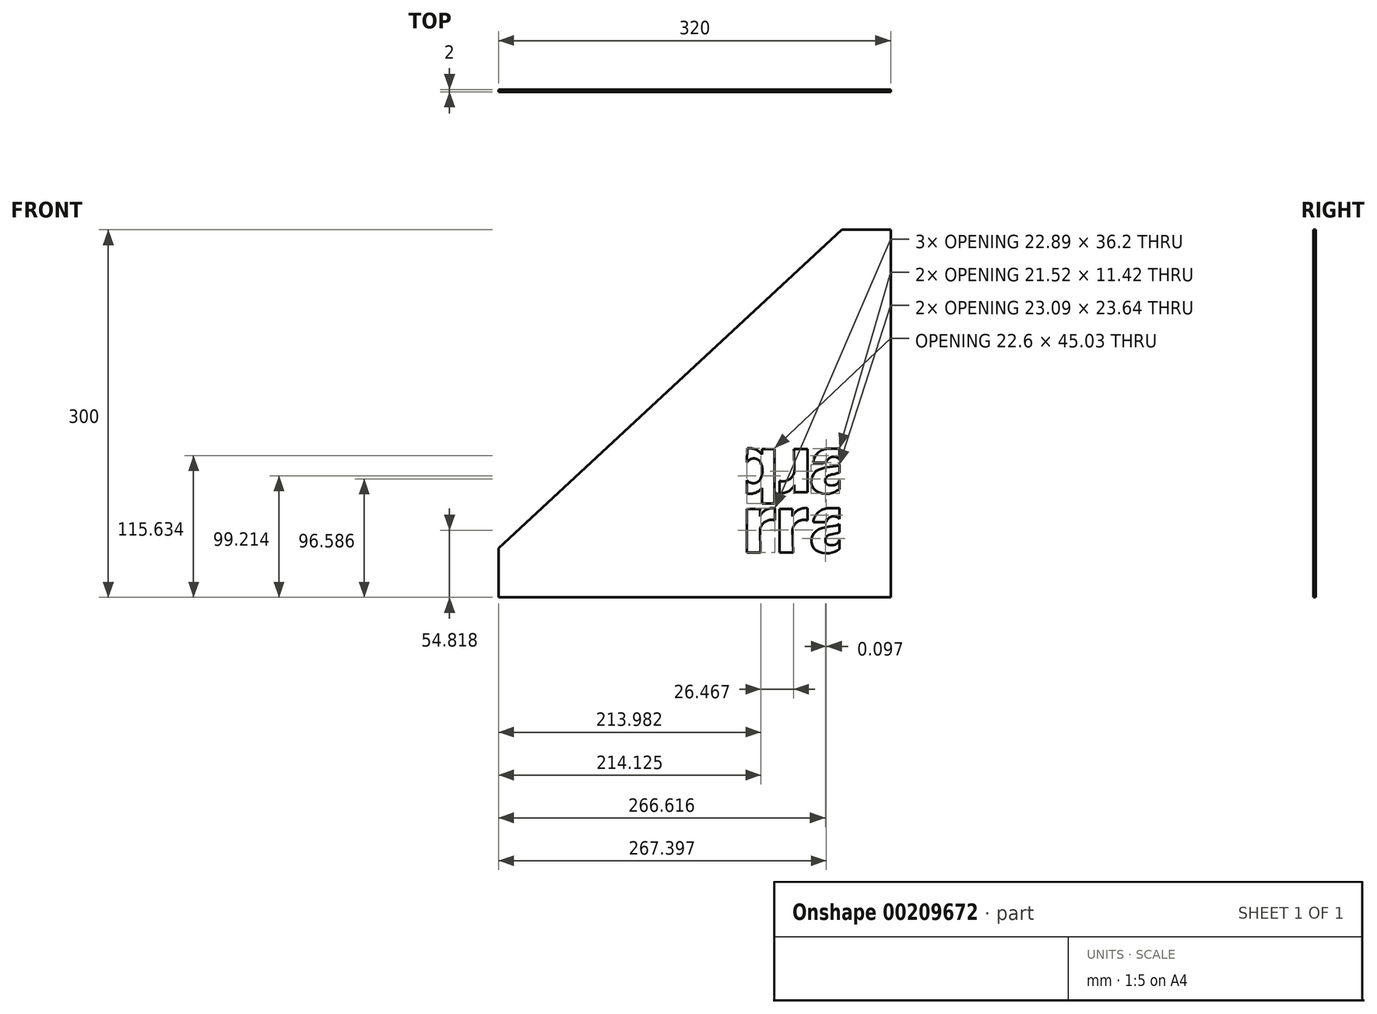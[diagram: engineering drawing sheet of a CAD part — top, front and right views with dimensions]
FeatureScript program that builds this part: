
annotation { "Feature Type Name" : "Feature", "Feature Type Description" : "" }
export const myFeature = defineFeature(function(context is Context, id is Id, definition is map)
    precondition{}
    {
        {
            var Q0;
            Q0=qCreatedBy(makeId("Front.planeOp"),FACE);
            var sketch = newSketch(context, id + "F0", { "sketchPlane" : qUnion([Q0])});
            skLineSegment(sketch, "E0.bottom", {"start": v(207.86, 33) * mm, "end": v(-112.14, 33) * mm});
            skLineSegment(sketch, "E0.top", {"start": v(207.86, 333) * mm, "end": v(167.86, 333) * mm});
            skLineSegment(sketch, "E0.left", {"start": v(207.86, 32.3) * mm, "end": v(207.86, 332.3) * mm});
            skLineSegment(sketch, "E0.right", {"start": v(-112.14, 33) * mm, "end": v(-112.14, 73) * mm});
            skPoint(sketch, "E0.middle", {"position": v(47.86, 183) * mm});
            skPoint(sketch, "E1", {"position": v(-112.14, 73) * mm});
            skPoint(sketch, "E2", {"position": v(167.86, 333) * mm});
            skLineSegment(sketch, "E3", {"start": v(167.86, 333) * mm, "end": v(-112.14, 73) * mm});
            skPoint(sketch, "E4.orphan", {"position": v(-112.14, 333) * mm});
            skArc(sketch, "E5", {"start": v(102.83, 149.58) * mm, "mid": v(97.48, 153.72) * mm, "end": v(90.77, 154.62) * mm});
            skLineSegment(sketch, "E6", {"start": v(102.83, 149.58) * mm, "end": v(102.83, 154.18) * mm});
            skLineSegment(sketch, "E7", {"start": v(102.83, 154.18) * mm, "end": v(113.14, 154.18) * mm});
            skLineSegment(sketch, "E8", {"start": v(113.14, 154.18) * mm, "end": v(113.14, 109.7) * mm});
            skLineSegment(sketch, "E9", {"start": v(113.14, 109.7) * mm, "end": v(102.83, 109.7) * mm});
            skLineSegment(sketch, "E10", {"start": v(102.83, 109.7) * mm, "end": v(102.83, 122.13) * mm});
            skArc(sketch, "E11", {"start": v(90.54, 117.53) * mm, "mid": v(97.27, 118.27) * mm, "end": v(102.83, 122.13) * mm});
            skLineSegment(sketch, "E12", {"start": v(90.54, 117.53) * mm, "end": v(90.54, 128.53) * mm});
            skArc(sketch, "E13", {"start": v(90.54, 128.53) * mm, "mid": v(96.4, 126.17) * mm, "end": v(101.68, 129.6) * mm});
            skArc(sketch, "E14", {"start": v(101.68, 129.6) * mm, "mid": v(103.2, 136.36) * mm, "end": v(101.68, 143.11) * mm});
            skArc(sketch, "E15", {"start": v(101.68, 143.11) * mm, "mid": v(96.14, 146.34) * mm, "end": v(90.6, 143.11) * mm});
            skLineSegment(sketch, "E16", {"start": v(90.77, 154.62) * mm, "end": v(90.6, 143.11) * mm});
            skLineSegment(sketch, "E17", {"start": v(128.82, 154.18) * mm, "end": v(139.9, 154.18) * mm});
            skLineSegment(sketch, "E18", {"start": v(139.9, 154.18) * mm, "end": v(139.9, 118.78) * mm});
            skLineSegment(sketch, "E19", {"start": v(139.9, 118.78) * mm, "end": v(129.27, 118.78) * mm});
            skLineSegment(sketch, "E20", {"start": v(129.27, 118.78) * mm, "end": v(129.27, 124.69) * mm});
            skArc(sketch, "E21", {"start": v(117, 118.08) * mm, "mid": v(124.2, 119.4) * mm, "end": v(129.27, 124.69) * mm});
            skLineSegment(sketch, "E22", {"start": v(117, 118.08) * mm, "end": v(117, 128.08) * mm});
            skArc(sketch, "E23", {"start": v(117, 128.08) * mm, "mid": v(124.75, 129.04) * mm, "end": v(129.23, 135.42) * mm});
            skLineSegment(sketch, "E24", {"start": v(128.82, 154.18) * mm, "end": v(129.23, 135.42) * mm});
            skArc(sketch, "E25", {"start": v(157.26, 154.35) * mm, "mid": v(148.72, 151.13) * mm, "end": v(144.5, 143.03) * mm});
            skLineSegment(sketch, "E26", {"start": v(157.26, 154.35) * mm, "end": v(166.02, 154.3) * mm});
            skLineSegment(sketch, "E27", {"start": v(166.02, 154.3) * mm, "end": v(166.02, 145.47) * mm});
            skArc(sketch, "E28", {"start": v(166.02, 145.47) * mm, "mid": v(159.78, 147.58) * mm, "end": v(155.12, 142.92) * mm});
            skLineSegment(sketch, "E29", {"start": v(155.12, 142.92) * mm, "end": v(144.5, 143.03) * mm});
            skFitSpline(sketch, "E30", {"points": [v(166.02, 141.4) * mm, v(160.69, 139.7) * mm, v(148.06, 136.68) * mm, v(142.95, 128.32) * mm, v(146.9, 119.87) * mm, v(158.9, 117.78) * mm, v(166.02, 121.11) * mm], "startDerivative": vector(-36.18, -29.19) * mm, "endDerivative": vector(54.96, 28.77) * mm});
            skLineSegment(sketch, "E31", {"start": v(166.02, 121.11) * mm, "end": v(166.02, 128.78) * mm});
            skFitSpline(sketch, "E32", {"points": [v(166.02, 128.78) * mm, v(164.1, 125.45) * mm, v(159.18, 124.28) * mm, v(155.03, 125.84) * mm, v(154.88, 130.56) * mm, v(158.9, 133.04) * mm, v(166.02, 134.74) * mm], "startDerivative": vector(-9.57, -26.3) * mm, "endDerivative": vector(42.8, 14.9) * mm});
            skLineSegment(sketch, "E33", {"start": v(166.02, 141.4) * mm, "end": v(166.02, 134.74) * mm});
            skLineSegment(sketch, "E34", {"start": v(101.61, 69.72) * mm, "end": v(90.54, 69.72) * mm});
            skLineSegment(sketch, "E35", {"start": v(90.54, 69.72) * mm, "end": v(90.54, 105.12) * mm});
            skLineSegment(sketch, "E36", {"start": v(90.54, 105.12) * mm, "end": v(101.17, 105.12) * mm});
            skLineSegment(sketch, "E37", {"start": v(101.17, 105.12) * mm, "end": v(101.17, 99.21) * mm});
            skArc(sketch, "E38", {"start": v(113.43, 105.82) * mm, "mid": v(106.23, 104.5) * mm, "end": v(101.17, 99.21) * mm});
            skLineSegment(sketch, "E39", {"start": v(113.43, 105.82) * mm, "end": v(113.43, 95.82) * mm});
            skArc(sketch, "E40", {"start": v(113.43, 95.82) * mm, "mid": v(105.69, 94.86) * mm, "end": v(101.2, 88.48) * mm});
            skLineSegment(sketch, "E41", {"start": v(101.61, 69.72) * mm, "end": v(101.2, 88.48) * mm});
            skLineSegment(sketch, "E42", {"start": v(128.1, 69.73) * mm, "end": v(117.03, 69.73) * mm});
            skLineSegment(sketch, "E43", {"start": v(117.03, 69.73) * mm, "end": v(117.03, 105.14) * mm});
            skLineSegment(sketch, "E44", {"start": v(117.03, 105.14) * mm, "end": v(127.66, 105.14) * mm});
            skLineSegment(sketch, "E45", {"start": v(127.66, 105.14) * mm, "end": v(127.66, 99.23) * mm});
            skArc(sketch, "E46", {"start": v(139.91, 105.84) * mm, "mid": v(132.72, 104.51) * mm, "end": v(127.66, 99.23) * mm});
            skLineSegment(sketch, "E47", {"start": v(139.91, 105.84) * mm, "end": v(139.91, 95.84) * mm});
            skArc(sketch, "E48", {"start": v(139.91, 95.84) * mm, "mid": v(132.17, 94.87) * mm, "end": v(127.69, 88.5) * mm});
            skLineSegment(sketch, "E49", {"start": v(128.1, 69.73) * mm, "end": v(127.69, 88.5) * mm});
            skArc(sketch, "E50", {"start": v(157.35, 105.72) * mm, "mid": v(148.81, 102.5) * mm, "end": v(144.6, 94.4) * mm});
            skLineSegment(sketch, "E51", {"start": v(157.35, 105.72) * mm, "end": v(166.12, 105.69) * mm});
            skLineSegment(sketch, "E52", {"start": v(166.12, 105.69) * mm, "end": v(166.12, 96.85) * mm});
            skArc(sketch, "E53", {"start": v(166.12, 96.85) * mm, "mid": v(159.88, 98.96) * mm, "end": v(155.22, 94.3) * mm});
            skLineSegment(sketch, "E54", {"start": v(155.22, 94.3) * mm, "end": v(144.6, 94.4) * mm});
            skFitSpline(sketch, "E55", {"points": [v(166.12, 92.78) * mm, v(160.78, 91.08) * mm, v(148.16, 88.06) * mm, v(143.05, 79.7) * mm, v(147, 71.25) * mm, v(159, 69.16) * mm, v(166.12, 72.49) * mm], "startDerivative": vector(-36.18, -29.19) * mm, "endDerivative": vector(54.96, 28.77) * mm});
            skLineSegment(sketch, "E56", {"start": v(166.12, 72.49) * mm, "end": v(166.12, 80.16) * mm});
            skFitSpline(sketch, "E57", {"points": [v(166.12, 80.16) * mm, v(164.2, 76.83) * mm, v(159.28, 75.66) * mm, v(155.13, 77.21) * mm, v(154.98, 81.94) * mm, v(159, 84.42) * mm, v(166.12, 86.12) * mm], "startDerivative": vector(-9.57, -26.3) * mm, "endDerivative": vector(42.8, 14.9) * mm});
            skLineSegment(sketch, "E58", {"start": v(166.12, 92.78) * mm, "end": v(166.12, 86.12) * mm});
            skLineSegment(sketch, "E59", {"start": v(-112.14, 33) * mm, "end": v(207.86, 33) * mm});
            skLineSegment(sketch, "E60", {"start": v(207.86, 333) * mm, "end": v(207.86, 33) * mm});
            skSolve(sketch);
        }
        {
            var Q0;
            Q0 = qSketchRegion(id + "F0", true);
            extrude(context, id + "F1", {"entities" : qUnion([Q0]), "depth" : 2 * mm});
        }
    });
